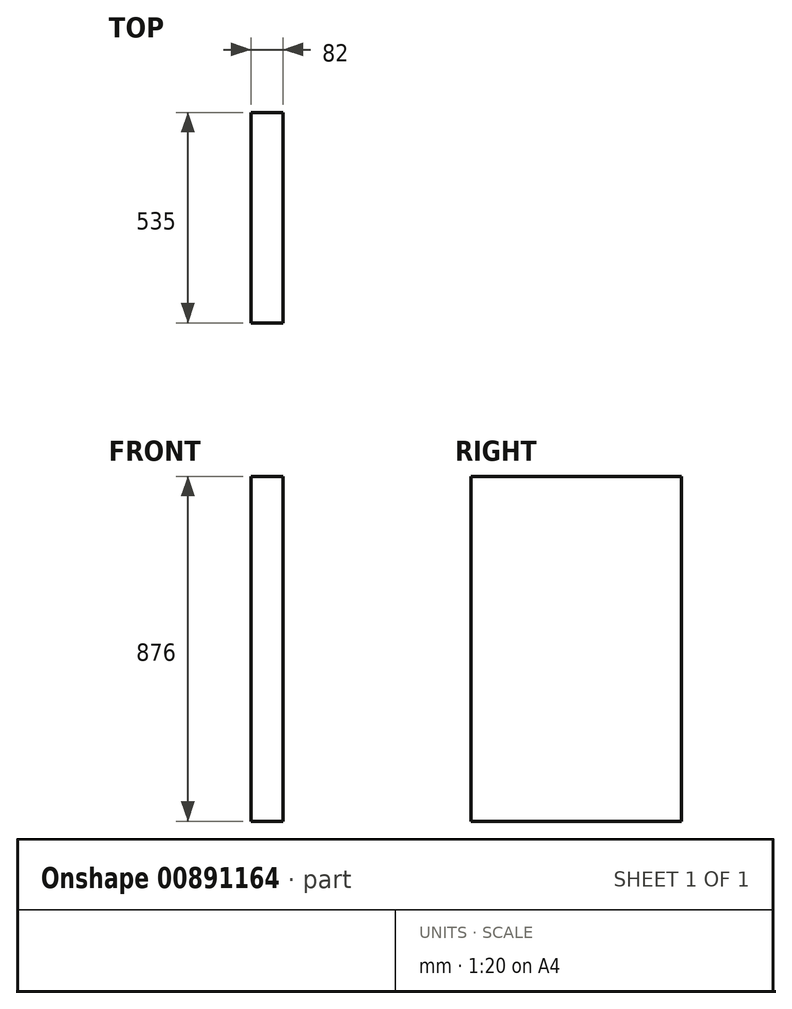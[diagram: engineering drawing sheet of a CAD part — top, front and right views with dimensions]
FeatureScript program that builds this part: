
annotation { "Feature Type Name" : "Feature", "Feature Type Description" : "" }
export const myFeature = defineFeature(function(context is Context, id is Id, definition is map)
    precondition{}
    {
        {
            var Q0;
            Q0=qCreatedBy(makeId("Front.planeOp"),FACE);
            var sketch = newSketch(context, id + "F0", { "sketchPlane" : qUnion([Q0])});
            skLineSegment(sketch, "E0.bottom", {"start": v(-60.12, -268.97) * mm, "end": v(21.88, -268.97) * mm});
            skLineSegment(sketch, "E0.top", {"start": v(-60.12, 607.03) * mm, "end": v(21.88, 607.03) * mm});
            skLineSegment(sketch, "E0.left", {"start": v(-60.12, -268.97) * mm, "end": v(-60.12, 607.03) * mm});
            skLineSegment(sketch, "E0.right", {"start": v(21.88, -268.97) * mm, "end": v(21.88, 607.03) * mm});
            skSolve(sketch);
        }
        {
            var Q0;
            Q0=makeQuery(id+"F0.imprint","IMPRINT",FACE,{"disambiguationData":[TD([[makeQuery(id+"F0.imprint","IMPRINT",EDGE,{"derivedFrom":sQuery(id+"F0.wireOp",EDGE,"E0.bottom")}),1.0]])]});
            extrude(context, id + "F1", {"entities" : qUnion([Q0]), "depth" : 535 * mm, "offsetDistance" : 25 * mm});
        }
    });
